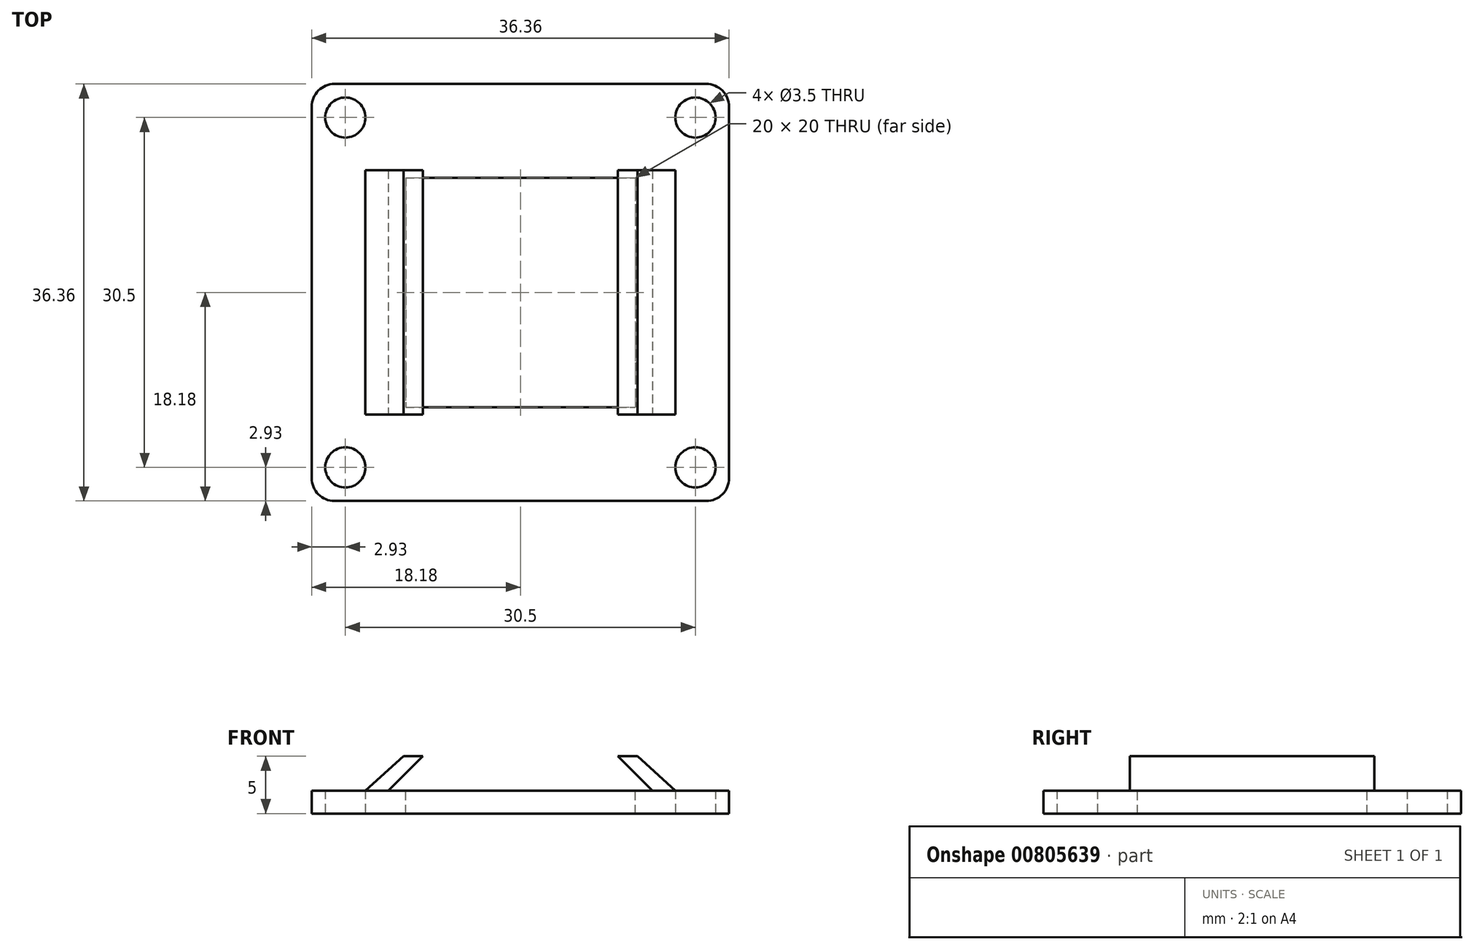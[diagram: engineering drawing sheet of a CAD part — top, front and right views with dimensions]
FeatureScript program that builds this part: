
annotation { "Feature Type Name" : "Feature", "Feature Type Description" : "" }
export const myFeature = defineFeature(function(context is Context, id is Id, definition is map)
    precondition{}
    {
        {
            var Q0;
            Q0=qCreatedBy(makeId("Top.planeOp"),FACE);
            var sketch = newSketch(context, id + "F0", { "sketchPlane" : qUnion([Q0])});
            skLineSegment(sketch, "E0.bottom", {"start": v(-15.25, 15.25) * mm, "end": v(15.25, 15.25) * mm});
            skLineSegment(sketch, "E0.top", {"start": v(-15.25, -15.25) * mm, "end": v(15.25, -15.25) * mm});
            skLineSegment(sketch, "E0.left", {"start": v(-15.25, 15.25) * mm, "end": v(-15.25, -15.25) * mm});
            skLineSegment(sketch, "E0.right", {"start": v(15.25, 15.25) * mm, "end": v(15.25, -15.25) * mm});
            skPoint(sketch, "E0.middle", {"position": v(0, 0) * mm});
            skCircle(sketch, "E1", {"center": v(-15.25, 15.25) * mm, "radius": 1.75 * mm});
            skCircle(sketch, "E2", {"center": v(15.25, 15.25) * mm, "radius": 1.75 * mm});
            skCircle(sketch, "E3", {"center": v(15.25, -15.25) * mm, "radius": 1.75 * mm});
            skCircle(sketch, "E4", {"center": v(-15.25, -15.25) * mm, "radius": 1.75 * mm});
            skLineSegment(sketch, "E5.bottom", {"start": v(-18.18, 18.18) * mm, "end": v(18.18, 18.18) * mm});
            skLineSegment(sketch, "E5.top", {"start": v(-18.18, -18.18) * mm, "end": v(18.18, -18.18) * mm});
            skLineSegment(sketch, "E5.left", {"start": v(-18.18, 18.18) * mm, "end": v(-18.18, -18.18) * mm});
            skLineSegment(sketch, "E5.right", {"start": v(18.18, 18.18) * mm, "end": v(18.18, -18.18) * mm});
            skCircle(sketch, "E6", {"center": v(-15.25, 15.25) * mm, "radius": 2.5 * mm, "construction": true});
            skSolve(sketch);
        }
        {
            var Q0;
            Q0 = qSketchRegion(id + "F0", true);
            var Q1;
            {var subQ5=sQuery(id+"F0.wireOp",EDGE,"E1");var subQ13=sQuery(id+"F0.wireOp",EDGE,"E0.bottom");var subQ14=makeQuery(id+"F0.imprint","INTERSECT",VERTEX,{"derivedFrom":[subQ13,subQ5]});Q1=makeQuery(id+"F0.imprint","IMPRINT",FACE,{"disambiguationData":[TD([[makeQuery(id+"F0.imprint","IMPRINT",EDGE,{"disambiguationData":[TD([[subQ14,-1.0]])],"derivedFrom":subQ13}),-1.0]])]});}
            extrude(context, id + "F1", {"entities" : qUnion([Q0, Q1]), "depth" : 2 * mm, "offsetDistance" : 25 * mm});
        }
        {
            var Q0;
            Q0=makeQuery(id+"F1.opExtrude","SWEPT_EDGE",EDGE,{"disambiguationData":[OSD([sQuery(id+"F0.wireOp",EDGE,"E5.bottom"),sQuery(id+"F0.wireOp",EDGE,"E5.left")])]});
            var Q1;
            Q1=makeQuery(id+"F1.opExtrude","SWEPT_EDGE",EDGE,{"disambiguationData":[OSD([sQuery(id+"F0.wireOp",EDGE,"E5.top"),sQuery(id+"F0.wireOp",EDGE,"E5.left")])]});
            var Q2;
            Q2=makeQuery(id+"F1.opExtrude","SWEPT_EDGE",EDGE,{"disambiguationData":[OSD([sQuery(id+"F0.wireOp",EDGE,"E5.bottom"),sQuery(id+"F0.wireOp",EDGE,"E5.right")])]});
            var Q3;
            Q3=makeQuery(id+"F1.opExtrude","SWEPT_EDGE",EDGE,{"disambiguationData":[OSD([sQuery(id+"F0.wireOp",EDGE,"E5.top"),sQuery(id+"F0.wireOp",EDGE,"E5.right")])]});
            fillet(context, id + "F2", {"entities" : qUnion([Q0, Q1, Q2, Q3]), "radius" : 2 * mm, "tangentPropagation" : true, "allowEdgeOverflow" : false});
        }
        {
            var Q0;
            Q0=makeQuery(id+"F1.opExtrude","CAP_FACE",FACE,{"disambiguationData":[OSD([sQuery(id+"F0.wireOp",EDGE,"E1"),sQuery(id+"F0.wireOp",EDGE,"E2"),sQuery(id+"F0.wireOp",EDGE,"E3"),sQuery(id+"F0.wireOp",EDGE,"E4"),sQuery(id+"F0.wireOp",EDGE,"E5.bottom"),sQuery(id+"F0.wireOp",EDGE,"E5.top"),sQuery(id+"F0.wireOp",EDGE,"E5.left"),sQuery(id+"F0.wireOp",EDGE,"E5.right")])],"isStart":false});
            var sketch = newSketch(context, id + "F3", { "sketchPlane" : qUnion([Q0])});
            skLineSegment(sketch, "E7.bottom", {"start": v(-10, 10) * mm, "end": v(10, 10) * mm});
            skLineSegment(sketch, "E7.top", {"start": v(-10, -10) * mm, "end": v(10, -10) * mm});
            skLineSegment(sketch, "E7.left", {"start": v(-10, 10) * mm, "end": v(-10, -10) * mm});
            skLineSegment(sketch, "E7.right", {"start": v(10, 10) * mm, "end": v(10, -10) * mm});
            skPoint(sketch, "E7.middle", {"position": v(0, 0) * mm});
            skSolve(sketch);
        }
        {
            var Q0;
            Q0 = qSketchRegion(id + "F3", true);
            extrude(context, id + "F4", {"entities" : qUnion([Q0]), "operationType" : NewBodyOperationType.REMOVE, "oppositeDirection" : true, "depth" : 25 * mm, "offsetDistance" : 25 * mm});
        }
        {
            var Q0;
            Q0=makeQuery(id+"F1.opExtrude","CAP_FACE",FACE,{"disambiguationData":[OSD([sQuery(id+"F0.wireOp",EDGE,"E1"),sQuery(id+"F0.wireOp",EDGE,"E2"),sQuery(id+"F0.wireOp",EDGE,"E3"),sQuery(id+"F0.wireOp",EDGE,"E4"),sQuery(id+"F0.wireOp",EDGE,"E5.bottom"),sQuery(id+"F0.wireOp",EDGE,"E5.top"),sQuery(id+"F0.wireOp",EDGE,"E5.left"),sQuery(id+"F0.wireOp",EDGE,"E5.right")])],"isStart":false});
            var sketch = newSketch(context, id + "F5", { "sketchPlane" : qUnion([Q0])});
            skLineSegment(sketch, "E8.bottom", {"start": v(-13.5, 10.65) * mm, "end": v(-11.5, 10.65) * mm});
            skLineSegment(sketch, "E8.top", {"start": v(-13.5, -10.65) * mm, "end": v(-11.5, -10.65) * mm});
            skLineSegment(sketch, "E8.left", {"start": v(-13.5, 10.65) * mm, "end": v(-13.5, -10.65) * mm});
            skLineSegment(sketch, "E8.right", {"start": v(-11.5, 10.65) * mm, "end": v(-11.5, -10.65) * mm});
            skPoint(sketch, "E8.middle", {"position": v(-12.5, 0) * mm});
            skLineSegment(sketch, "E9.MirrorCS", {"start": v(11.5, 10.65) * mm, "end": v(11.5, -10.65) * mm});
            skLineSegment(sketch, "E10.MirrorCS", {"start": v(13.5, 10.65) * mm, "end": v(13.5, -10.65) * mm});
            skLineSegment(sketch, "E11.MirrorCS", {"start": v(13.5, 10.65) * mm, "end": v(11.5, 10.65) * mm});
            skLineSegment(sketch, "E12.MirrorCS", {"start": v(13.5, -10.65) * mm, "end": v(11.5, -10.65) * mm});
            skSolve(sketch);
        }
        {
            var Q0;
            Q0=makeQuery(id+"F5.imprint","IMPRINT",FACE,{"disambiguationData":[TD([[makeQuery(id+"F5.imprint","IMPRINT",EDGE,{"derivedFrom":sQuery(id+"F5.wireOp",EDGE,"E8.bottom")}),1.0]])]});
            cPlane(context, id + "F6", {"entities" : qUnion([Q0]), "cplaneType" : CPlaneType.OFFSET, "offset" : 3 * mm, "width" : 150 * mm, "height" : 150 * mm});
        }
        {
            var Q0;
            Q0=qCreatedBy(id+"F6.planeOp",FACE);
            var sketch = newSketch(context, id + "F7", { "sketchPlane" : qUnion([Q0])});
            skLineSegment(sketch, "E13.bottom", {"start": v(-10.2, 10.65) * mm, "end": v(-8.5, 10.65) * mm});
            skLineSegment(sketch, "E13.top", {"start": v(-10.2, -10.65) * mm, "end": v(-8.5, -10.65) * mm});
            skLineSegment(sketch, "E13.left", {"start": v(-10.2, 10.65) * mm, "end": v(-10.2, -10.65) * mm});
            skLineSegment(sketch, "E13.right", {"start": v(-8.5, 10.65) * mm, "end": v(-8.5, -10.65) * mm});
            skPoint(sketch, "E13.middle", {"position": v(-9.35, 0) * mm});
            skLineSegment(sketch, "E14.MirrorCS", {"start": v(8.5, 10.65) * mm, "end": v(8.5, -10.65) * mm});
            skLineSegment(sketch, "E15.MirrorCS", {"start": v(10.2, 10.65) * mm, "end": v(8.5, 10.65) * mm});
            skLineSegment(sketch, "E16.MirrorCS", {"start": v(10.2, 10.65) * mm, "end": v(10.2, -10.65) * mm});
            skLineSegment(sketch, "E17.MirrorCS", {"start": v(10.2, -10.65) * mm, "end": v(8.5, -10.65) * mm});
            skSolve(sketch);
        }
        {
            var Q1;
            Q1=makeQuery(id+"F5.imprint","IMPRINT",FACE,{"disambiguationData":[TD([[makeQuery(id+"F5.imprint","IMPRINT",EDGE,{"derivedFrom":sQuery(id+"F5.wireOp",EDGE,"E8.bottom")}),-1.0]])]});
            var Q2;
            Q2=makeQuery(id+"F7.imprint","IMPRINT",FACE,{"disambiguationData":[TD([[makeQuery(id+"F7.imprint","IMPRINT",EDGE,{"derivedFrom":sQuery(id+"F7.wireOp",EDGE,"E13.bottom")}),-1.0]])]});
            loft(context, id + "F8", {"operationType" : NewBodyOperationType.ADD, "sheetProfilesArray" : [{ "sheetProfileEntities" : qUnion([Q1]) }, { "sheetProfileEntities" : qUnion([Q2]) }]});
        }
        {
            var Q1;
            Q1=makeQuery(id+"F5.imprint","IMPRINT",FACE,{"disambiguationData":[TD([[makeQuery(id+"F5.imprint","IMPRINT",EDGE,{"derivedFrom":sQuery(id+"F5.wireOp",EDGE,"E9.MirrorCS")}),1.0]])]});
            var Q2;
            Q2=makeQuery(id+"F7.imprint","IMPRINT",FACE,{"disambiguationData":[TD([[makeQuery(id+"F7.imprint","IMPRINT",EDGE,{"derivedFrom":sQuery(id+"F7.wireOp",EDGE,"E14.MirrorCS")}),1.0]])]});
            loft(context, id + "F9", {"operationType" : NewBodyOperationType.ADD, "sheetProfilesArray" : [{ "sheetProfileEntities" : qUnion([Q1]) }, { "sheetProfileEntities" : qUnion([Q2]) }]});
        }
    });
